# Revit family: ROTHOB_Rothoblaas_Tape_InvisiBand
name_source: partatom
category: Structural Connections
units: mm (PartAtom-declared; Revit-internal decimal feet)

## family parameters
Cut with Voids When Loaded = No
Enable cutting in views = Yes
Host = Face
Material for Model Behavior = Other
OmniClass Number = 23.13.23.17
OmniClass Title = General Purpose Tape
Shared = No

## types (1)
- INVISI BAND
    AdhesionStrengthOSB_180°_10minutes = 10,0 N/10 mm
    AdhesionStrengthOSB_90°_10minutes = 4,5 N/10 mm
    AdhesionStrength_Average_PP_Membrane_24hours = 25,0 N/50 mm
    ApplicationTemperature = -10/+35 °C
    BIMObjectName = ROTHOB_Rothoblaas_Tape_InvisiBand
    Category = Pr_35_90_87_02 - Acrylic adhesive sealant tapes
    Color = Transparent
    Default Elevation = 1.22 m
    Description = Transparent single-sided adhesive tape without liner, resistant to UV and high temperatures
    DurationUnit = Years
    Esporta tipo in formato IFC con nome = IfcBuildingElementProxyType
    ExposureWeather = 12 months
    Finish = PE special film
    FireResistanceRating_PlainCLT_100mm_5mm_Joint_Combined with joint cover board = EI 90
    IfcExportAs = IfcBuildingElementProxyType
    IfcExportType = USERDEFINED
    ManufacturerName = ROTHO BLAAS SRL
    ManufacturerURL = www.rothoblaas.com
    Material = Polyethylene
    ModelDisclaimer = The latest version of the data sheets can be found on our website
    Name = Tape
    ObjectMaterial = ROTHOB_Rothoblaas_Polyethylene
    OmniClassCode = 23.13 23.17
    OmniClassTitle = General Purpose Tape
    OmniClassVersion = 2012-05-16
    ProductInformation = https://www.rothoblaas.com
    ResistanceTemperature = -30/+80 °C
    Shape = Bidimensional
    ShearAdhesionStrength_Joint_PP_Membrane_24hours = 70,0 N/50 mm
    Tipo IFC predefinito = USERDEFINED
    UniClass2015Code = Pr_35_90_87_02
    UniClass2015Title = Acrylic adhesive sealant tapes
    UniClass2015Version = Products v1.33
    Version = 1
